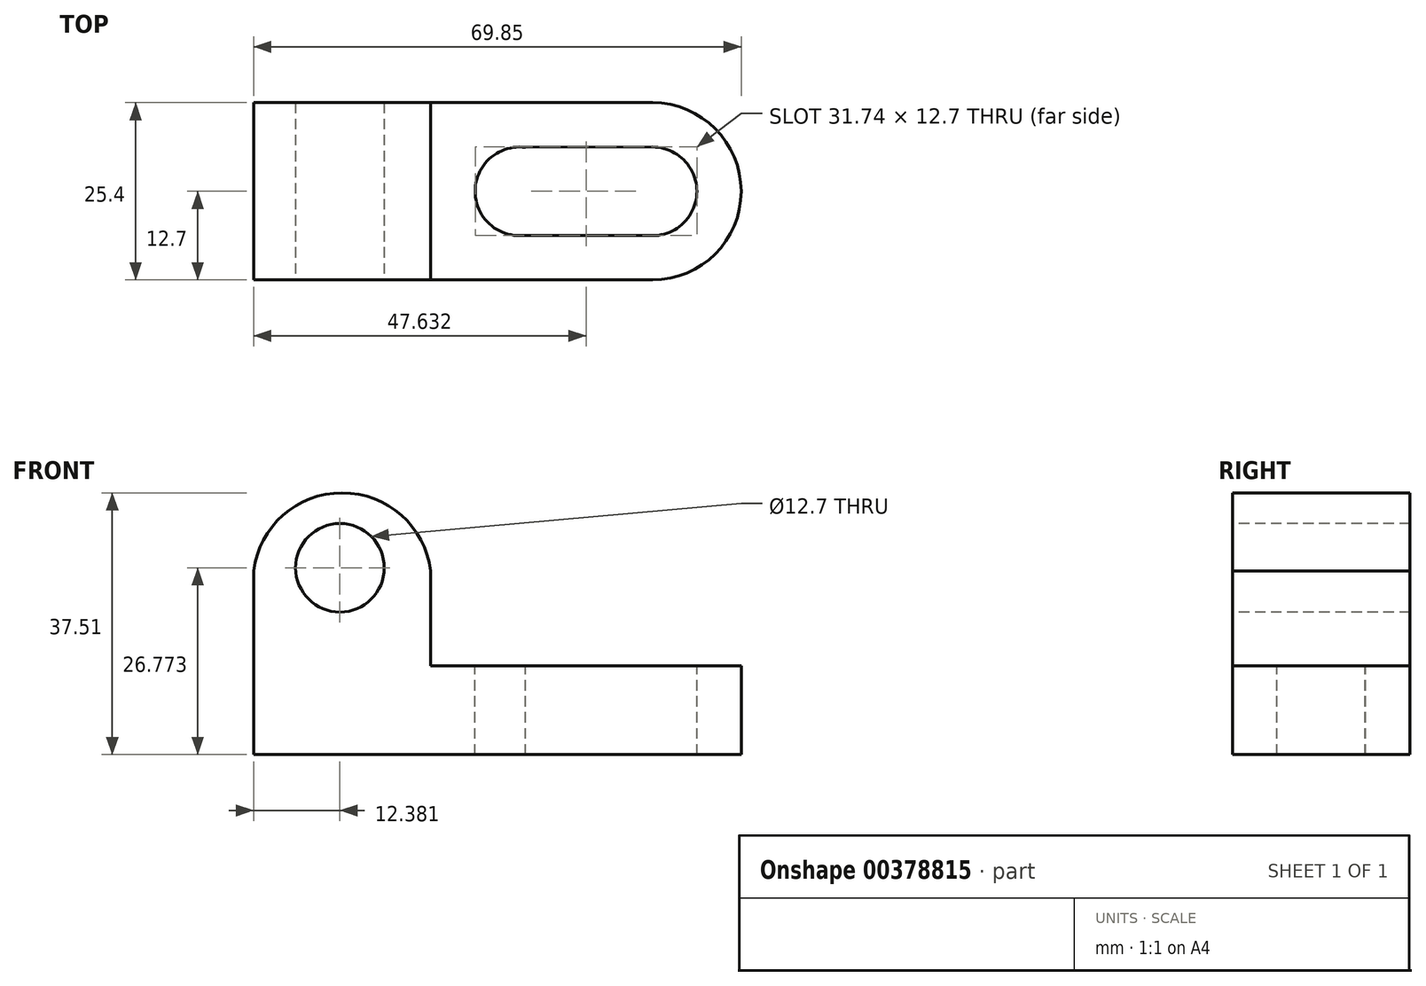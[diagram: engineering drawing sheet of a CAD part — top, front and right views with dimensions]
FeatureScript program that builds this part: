
annotation { "Feature Type Name" : "Feature", "Feature Type Description" : "" }
export const myFeature = defineFeature(function(context is Context, id is Id, definition is map)
    precondition{}
    {
        {
            var Q0;
            Q0=qCreatedBy(makeId("Front.planeOp"),FACE);
            var sketch = newSketch(context, id + "F0", { "sketchPlane" : qUnion([Q0])});
            skLineSegment(sketch, "E0", {"start": v(0, 0) * mm, "end": v(69.85, 0) * mm});
            skLineSegment(sketch, "E1", {"start": v(69.85, 0) * mm, "end": v(69.85, 12.7) * mm});
            skLineSegment(sketch, "E2", {"start": v(69.85, 12.7) * mm, "end": v(25.4, 12.7) * mm});
            skLineSegment(sketch, "E3", {"start": v(25.4, 12.7) * mm, "end": v(25.4, 38.1) * mm});
            skLineSegment(sketch, "E4", {"start": v(25.4, 38.1) * mm, "end": v(0, 38.1) * mm});
            skLineSegment(sketch, "E5", {"start": v(0, 38.1) * mm, "end": v(0, 0) * mm});
            skSolve(sketch);
        }
        {
            var Q0;
            Q0 = qSketchRegion(id + "F0", true);
            extrude(context, id + "F1", {"entities" : qUnion([Q0]), "depth" : 25.4 * mm});
        }
        {
            var Q0;
            Q0=makeQuery(id+"F1.opExtrude","CAP_FACE",FACE,{"disambiguationData":[OSD([sQuery(id+"F0.wireOp",EDGE,"E0"),sQuery(id+"F0.wireOp",EDGE,"E1"),sQuery(id+"F0.wireOp",EDGE,"E2"),sQuery(id+"F0.wireOp",EDGE,"E3"),sQuery(id+"F0.wireOp",EDGE,"E4"),sQuery(id+"F0.wireOp",EDGE,"E5")])],"isStart":false});
            var sketch = newSketch(context, id + "F2", { "sketchPlane" : qUnion([Q0])});
            skCircle(sketch, "E6", {"center": v(12.38, 26.77) * mm, "radius": 6.35 * mm});
            skSolve(sketch);
        }
        {
            var Q0;
            Q0=makeQuery(id+"F2.imprint","IMPRINT",FACE,{"disambiguationData":[TD([[makeQuery(id+"F2.imprint","IMPRINT",EDGE,{"derivedFrom":sQuery(id+"F2.wireOp",EDGE,"E6")}),1.0]])]});
            extrude(context, id + "F3", {"entities" : qUnion([Q0]), "operationType" : NewBodyOperationType.REMOVE, "oppositeDirection" : true, "depth" : 25.4 * mm});
        }
        {
            var Q0;
            Q0=makeQuery(id+"F1.opExtrude","CAP_FACE",FACE,{"disambiguationData":[OSD([sQuery(id+"F0.wireOp",EDGE,"E0"),sQuery(id+"F0.wireOp",EDGE,"E1"),sQuery(id+"F0.wireOp",EDGE,"E2"),sQuery(id+"F0.wireOp",EDGE,"E3"),sQuery(id+"F0.wireOp",EDGE,"E4"),sQuery(id+"F0.wireOp",EDGE,"E5")])],"isStart":false});
            var sketch = newSketch(context, id + "F4", { "sketchPlane" : qUnion([Q0])});
            skSolve(sketch);
        }
        {
            var Q0;
            Q0=makeQuery(id+"F1.opExtrude","SWEPT_FACE",FACE,{"disambiguationData":[OSD([sQuery(id+"F0.wireOp",EDGE,"E2")])]});
            var sketch = newSketch(context, id + "F5", { "sketchPlane" : qUnion([Q0])});
            skCircle(sketch, "E7", {"center": v(38.1, -12.7) * mm, "radius": 6.35 * mm});
            skCircle(sketch, "E8", {"center": v(57.15, -12.7) * mm, "radius": 6.35 * mm});
            skLineSegment(sketch, "E9", {"start": v(37.19, -6.42) * mm, "end": v(57.15, -6.35) * mm});
            skLineSegment(sketch, "E10", {"start": v(38.16, -19.05) * mm, "end": v(57.15, -19.05) * mm});
            skSolve(sketch);
        }
        {
            var Q0;
            Q0 = qSketchRegion(id + "F5", true);
            extrude(context, id + "F6", {"entities" : qUnion([Q0]), "operationType" : NewBodyOperationType.REMOVE, "oppositeDirection" : true, "depth" : 25.4 * mm});
        }
        {
            var Q0;
            Q0=makeQuery(id+"F1.opExtrude","SWEPT_FACE",FACE,{"disambiguationData":[OSD([sQuery(id+"F0.wireOp",EDGE,"E2")])]});
            var sketch = newSketch(context, id + "F7", { "sketchPlane" : qUnion([Q0])});
            skArc(sketch, "E11", {"start": v(57.15, -25.4) * mm, "mid": v(69.85, -12.7) * mm, "end": v(57.15, 0) * mm});
            skSolve(sketch);
        }
        {
            var Q0;
            Q0 = qSketchRegion(id + "F7", true);
            var Q1;
            {var subQ1=sQuery(id+"F0.wireOp",EDGE,"E2");var subQ6=makeQuery(id+"F1.opExtrude","SWEPT_EDGE",EDGE,{"disambiguationData":[OSD([sQuery(id+"F0.wireOp",EDGE,"E1"),subQ1])]});Q1=makeQuery(id+"F7.imprint","IMPRINT",FACE,{"disambiguationData":[TD([[makeQuery(id+"F7.imprint","IMPRINT",EDGE,{"derivedFrom":subQ6}),1.0]])]});}
            extrude(context, id + "F8", {"entities" : qUnion([Q0, Q1]), "operationType" : NewBodyOperationType.REMOVE, "oppositeDirection" : true, "depth" : 25.4 * mm});
        }
        {
            var Q0;
            Q0=makeQuery(id+"F4.imprint","IMPRINT",FACE,{"disambiguationData":[TD([[makeQuery(id+"F4.imprint","IMPRINT",EDGE,{"derivedFrom":makeQuery(id+"F1.opExtrude","CAP_EDGE",EDGE,{"disambiguationData":[OSD([sQuery(id+"F0.wireOp",EDGE,"E0")])],"isStart":false})}),1.0]])]});
            var sketch = newSketch(context, id + "F9", { "sketchPlane" : qUnion([Q0])});
            skArc(sketch, "E12", {"start": v(25.4, 23.1) * mm, "mid": v(12.7, 37.5) * mm, "end": v(0, 23.1) * mm});
            skSolve(sketch);
        }
        {
            var Q0;
            Q0 = qSketchRegion(id + "F9", true);
            var Q1;
            {var subQ5=makeQuery(id+"F4.imprint","IMPRINT",EDGE,{"derivedFrom":makeQuery(id+"F1.opExtrude","CAP_EDGE",EDGE,{"disambiguationData":[OSD([sQuery(id+"F0.wireOp",EDGE,"E4")])],"isStart":false})});Q1=makeQuery(id+"F9.imprint","IMPRINT",FACE,{"disambiguationData":[TD([[makeQuery(id+"F9.imprint","IMPRINT",EDGE,{"derivedFrom":subQ5}),1.0]])]});}
            extrude(context, id + "F10", {"entities" : qUnion([Q0, Q1]), "operationType" : NewBodyOperationType.REMOVE, "oppositeDirection" : true, "depth" : 25.4 * mm});
        }
    });
